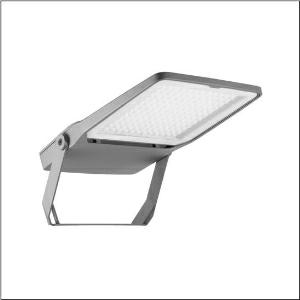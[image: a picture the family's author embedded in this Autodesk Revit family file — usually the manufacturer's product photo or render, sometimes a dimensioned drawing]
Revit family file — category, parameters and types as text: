
# Revit family: floodlight_fl_20_midi___pl61_5xa7682d2c1ac_8fda
name_source: partatom
category: Lighting Fixtures
units: mm (PartAtom-declared; Revit-internal decimal feet)

## family parameters
Cut with Voids When Loaded = No
Host = Face
Light Source = No
Part Type = Normal
Room Calculation Point = No
Round Connector Dimension = Use Diameter
Shared = No

## types (1)
- --- (1 x LED 4000K / CRI = 70 (unbekannt), 18200 lm, 4000K)
    Apparent Load = 142 VA
    CIE Flux Codes = 33 65 98 100 100
    Color Rendering = 70
    Color Temperature = 4000K
    Default Elevation = 1800 mm
    Description = Floodlight FL 20 midi, floodlight, primary light control with lens, of plastic, primary optical cover: protective disc, of toughened safety glass, transparent, light distribution: PL61, light emission: direct distribution, primary light characteristic: asymmetric, installation type: surface-mounted, LED, High Power LED, rated luminous flux: 18.200lm, luminous efficacy: 128lm/W, light colour: 740, colour temperature: 4000K, control gear: ECG Plus, control: flexible luminous flux parameterisation, time-dependent luminous flux control, digital communication interface, power reduction, overheat protection, electronic power reduction, with terminal, 5-pole, max. 2.5mm², mains connection: 220..240V, AC, 50/60Hz, rated input power: 142W, LED unit, of diecast aluminium, powder-coated, Siteco® metallic grey (DB 702S), corrosivity category C5 mid according to DIN EN ISO 12944, incl. 1x M20 cable gland for cable Ø 6.5..12mm, length: 654mm, width: 450mm, height: 76mm, housing frame, of diecast aluminium, powder-coated, Siteco® metallic grey (DB 702S), mounting bracket, of steel, powder-coated, Siteco® metallic grey (DB 702S), DALI, protection rating (complete): IP66, insulation class (complete): insulation class II (safety insulation), certification: CE, ENEC, VDE, protection symbol: D, permissible operating ambient temperature: -40..+40°C, permissible operating ambient temperature for outdoor applications: -40..+50°C, standard: DIN EN 12944, packaging unit: 1 piece

Light Distribution: PL61
    Height = 76 mm
    Lamp = 1 x LED 4000K / CRI >= 70 (unbekannt)
    Lamp Light Flux = 18200 lm
    Lamp count = 1
    Length = 672 mm
    Luminous efficacy = 128 lm/W
    Manufacturer = Siteco
    ModVariant = No
    Model = 5XA7682D2C1AC
    Mounting Place = Wall
    Mounting Type = Surface mounted
    Number of Poles = 1
    OnlyDefault = Yes
    Power Factor = 1
    Product Name = Floodlight FL 20 midi | PL61
    Product group = floodlight | wall mounted
    ProductGroupID = 2001
    Protection Class = Protection class II
    Protection Degree = IP 66
    RLX_Detail_Level = 1
    RLX_Emergency_Light_Flux = 0 lm
    RLX_Emergency_Type = 0
    RLX_Emergency_Type_DB = No
    RlxData = <blob elided: 97921 chars, md5=c341f6c6>
    Socket = socket
    Standby Power = 0 W
    System Light Flux = 18200 lm
    System Power = 142 W
    Type Comments = factory setting: luminous flux: 100 % | dim-lin: 254 | 489 mA
    Type Image = l_1005943.jpg
    URL = http://relux.com
    VarID = @adj_147279
    Voltage = 0 V
    Weight = 0.00 kg
    Width = 450 mm

## geometry (parser evidence)
native form markers: Blend x4, Sweep x12
no freeform markers — native parametric forms only
